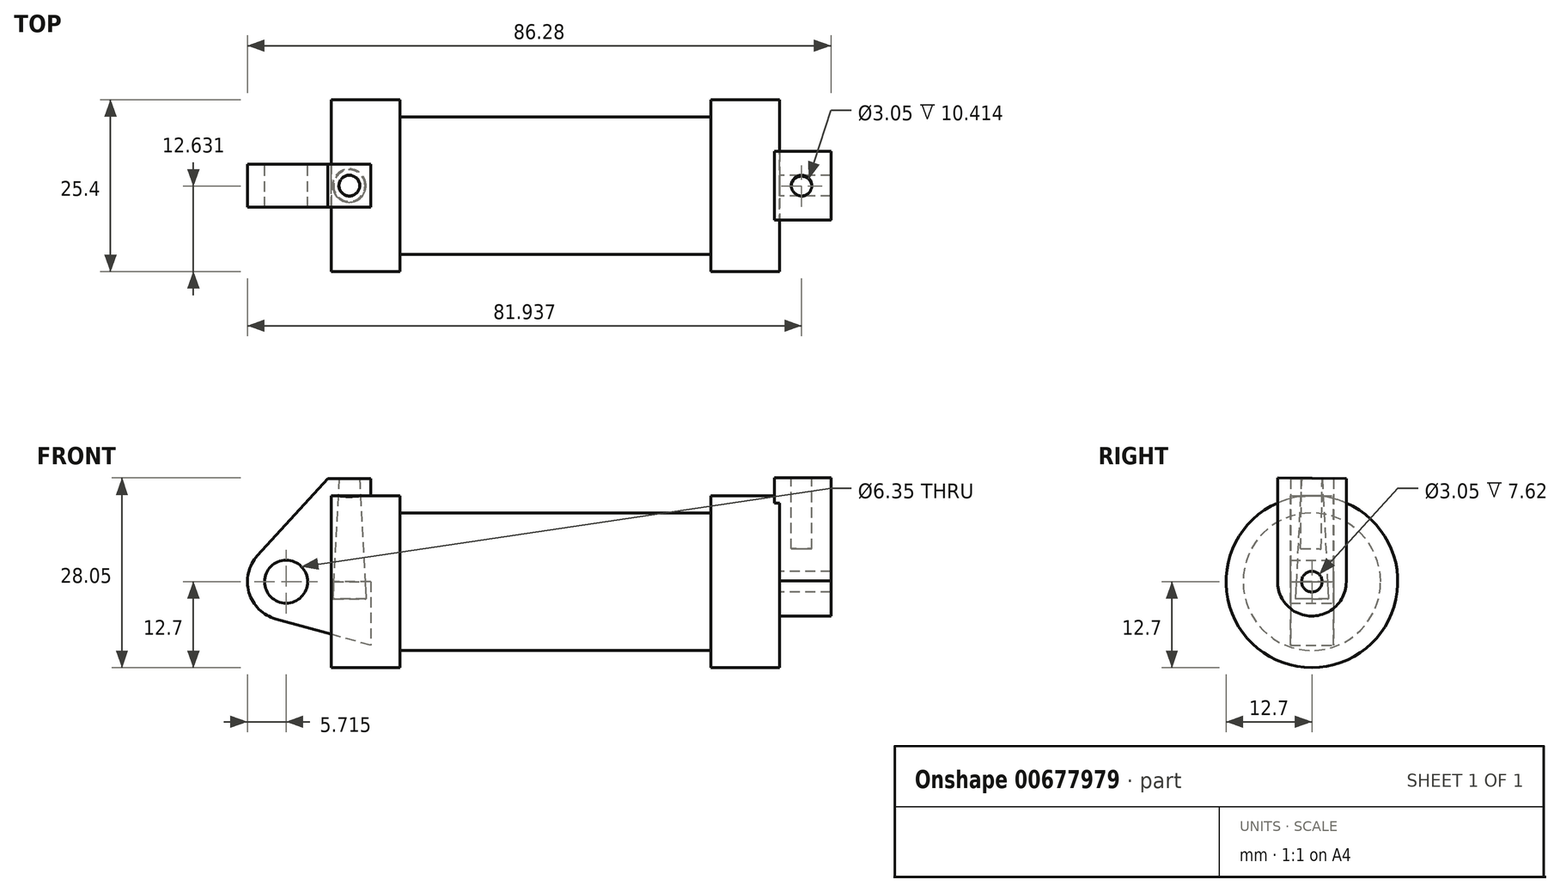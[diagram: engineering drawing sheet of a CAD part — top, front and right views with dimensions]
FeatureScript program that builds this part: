
annotation { "Feature Type Name" : "Feature", "Feature Type Description" : "" }
export const myFeature = defineFeature(function(context is Context, id is Id, definition is map)
    precondition{}
    {
        {
            var Q0;
            Q0=qCreatedBy(makeId("Front.planeOp"),FACE);
            var sketch = newSketch(context, id + "F0", { "sketchPlane" : qUnion([Q0])});
            skLineSegment(sketch, "E0", {"start": v(0, 0) * mm, "end": v(0, 12.7) * mm});
            skLineSegment(sketch, "E1", {"start": v(0, 12.7) * mm, "end": v(10.16, 12.7) * mm});
            skLineSegment(sketch, "E2", {"start": v(10.16, 12.7) * mm, "end": v(10.16, 10.16) * mm});
            skLineSegment(sketch, "E3", {"start": v(10.16, 10.16) * mm, "end": v(56.13, 10.16) * mm});
            skLineSegment(sketch, "E4", {"start": v(56.13, 10.16) * mm, "end": v(56.13, 12.7) * mm});
            skLineSegment(sketch, "E5", {"start": v(56.13, 12.7) * mm, "end": v(66.3, 12.7) * mm});
            skLineSegment(sketch, "E6", {"start": v(66.3, 12.7) * mm, "end": v(66.3, 0) * mm});
            skLineSegment(sketch, "E7", {"start": v(66.3, 0) * mm, "end": v(0, 0) * mm});
            skLineSegment(sketch, "E8", {"start": v(5.84, 15.24) * mm, "end": v(-0.5, 15.24) * mm});
            skLineSegment(sketch, "E9", {"start": v(-0.5, 15.24) * mm, "end": v(-10.88, 3.85) * mm});
            skLineSegment(sketch, "E10", {"start": v(0, 0) * mm, "end": v(-6.65, 0) * mm});
            skCircle(sketch, "E11", {"center": v(-6.65, 0) * mm, "radius": 5.72 * mm});
            skCircle(sketch, "E12", {"center": v(-6.65, 0) * mm, "radius": 3.18 * mm});
            skLineSegment(sketch, "E13", {"start": v(5.84, 15.24) * mm, "end": v(5.84, -9.4) * mm});
            skLineSegment(sketch, "E14", {"start": v(5.84, -9.4) * mm, "end": v(-8.18, -5.5) * mm});
            skSolve(sketch);
        }
        {
            var Q0;
            {var subQ0=sQuery(id+"F0.wireOp",EDGE,"E2");Q0=makeQuery(id+"F0.imprint","IMPRINT",FACE,{"disambiguationData":[TD([[makeQuery(id+"F0.imprint","IMPRINT",EDGE,{"derivedFrom":subQ0}),-1.0]])]});}
            var Q1;
            {var subQ0=sQuery(id+"F0.wireOp",EDGE,"E0");Q1=makeQuery(id+"F0.imprint","IMPRINT",FACE,{"disambiguationData":[TD([[makeQuery(id+"F0.imprint","IMPRINT",EDGE,{"derivedFrom":subQ0}),-1.0]])]});}
            var Q2;
            Q2=sQuery(id+"F0.wireOp",EDGE,"E7");
            revolve(context, id + "F1", {"entities" : qUnion([Q0, Q1]), "axis" : qUnion([Q2]), "revolveType" : RevolveType.FULL});
        }
        {
            var Q0;
            {var subQ1=sQuery(id+"F0.wireOp",EDGE,"E0");Q0=makeQuery(id+"F0.imprint","IMPRINT",FACE,{"disambiguationData":[TD([[makeQuery(id+"F0.imprint","IMPRINT",EDGE,{"derivedFrom":subQ1}),1.0]])]});}
            var Q1;
            {var subQ0=sQuery(id+"F0.wireOp",EDGE,"E14");Q1=makeQuery(id+"F0.imprint","IMPRINT",FACE,{"disambiguationData":[TD([[makeQuery(id+"F0.imprint","IMPRINT",EDGE,{"derivedFrom":subQ0}),-1.0]])]});}
            var Q2;
            {var subQ5=sQuery(id+"F0.wireOp",EDGE,"E12");Q2=makeQuery(id+"F0.imprint","IMPRINT",FACE,{"disambiguationData":[TD([[makeQuery(id+"F0.imprint","IMPRINT",EDGE,{"derivedFrom":subQ5}),-1.0]])]});}
            extrude(context, id + "F2", {"entities" : qUnion([Q0, Q1, Q2]), "endBound" : BoundingType.SYMMETRIC, "depth" : 6.35 * mm, "offsetDistance" : 25.4 * mm});
        }
        {
            var Q0;
            Q0=makeQuery(id+"F1.opRevolve","SWEPT_FACE",FACE,{"disambiguationData":[OSD([sQuery(id+"F0.wireOp",EDGE,"E6")])]});
            var sketch = newSketch(context, id + "F3", { "sketchPlane" : qUnion([Q0])});
            skCircle(sketch, "E15", {"center": v(0, 0) * mm, "radius": 1.52 * mm});
            skCircle(sketch, "E16", {"center": v(0, 0) * mm, "radius": 5.08 * mm});
            skLineSegment(sketch, "E17", {"start": v(-5.08, 0.11) * mm, "end": v(-5.08, 15.35) * mm});
            skLineSegment(sketch, "E18", {"start": v(5.08, -0.02) * mm, "end": v(5.08, 15.22) * mm});
            skLineSegment(sketch, "E19", {"start": v(5.08, 15.22) * mm, "end": v(-5.08, 15.35) * mm});
            skSolve(sketch);
        }
        {
            var Q0;
            Q0=makeQuery(id+"F3.imprint","IMPRINT",FACE,{"disambiguationData":[TD([[makeQuery(id+"F3.imprint","IMPRINT",EDGE,{"derivedFrom":sQuery(id+"F3.wireOp",EDGE,"E15")}),-1.0]])]});
            var Q1;
            {var subQ0=sQuery(id+"F3.wireOp",EDGE,"E19");Q1=makeQuery(id+"F3.imprint","IMPRINT",FACE,{"disambiguationData":[TD([[makeQuery(id+"F3.imprint","IMPRINT",EDGE,{"derivedFrom":subQ0}),1.0]])]});}
            var Q2;
            {var subQ0=sQuery(id+"F3.wireOp",EDGE,"E17");var subQ1=sQuery(id+"F3.wireOp",EDGE,"E16");var subQ2=makeQuery(id+"F3.imprint","INTERSECT",VERTEX,{"derivedFrom":[subQ1,subQ0]});Q2=makeQuery(id+"F3.imprint","IMPRINT",FACE,{"disambiguationData":[TD([[makeQuery(id+"F3.imprint","IMPRINT",EDGE,{"disambiguationData":[TD([[subQ2,1.0]])],"derivedFrom":subQ1}),-1.0]])]});}
            extrude(context, id + "F4", {"entities" : qUnion([Q0, Q1, Q2]), "operationType" : NewBodyOperationType.ADD, "depth" : 7.62 * mm, "offsetDistance" : 25.4 * mm, "hasSecondDirection" : true, "secondDirectionOppositeDirection" : true, "secondDirectionDepth" : 0.76 * mm});
        }
        {
            var Q0;
            Q0=makeQuery(id+"F2.opExtrude","SWEPT_FACE",FACE,{"disambiguationData":[OSD([sQuery(id+"F0.wireOp",EDGE,"E8")])]});
            var sketch = newSketch(context, id + "F5", { "sketchPlane" : qUnion([Q0])});
            skCircle(sketch, "E20", {"center": v(2.7, 0) * mm, "radius": 1.52 * mm});
            skPoint(sketch, "E20.centerSnap0", {"position": v(5.84, 0) * mm});
            skSolve(sketch);
        }
        {
            var Q0;
            Q0=makeQuery(id+"F5.imprint","IMPRINT",FACE,{"disambiguationData":[TD([[makeQuery(id+"F5.imprint","IMPRINT",EDGE,{"derivedFrom":sQuery(id+"F5.wireOp",EDGE,"E20")}),1.0]])]});
            var Q1;
            Q1=sQuery(id+"F5.wireOp",EDGE,"E20");
            extrude(context, id + "F6", {"entities" : qUnion([Q0]), "operationType" : NewBodyOperationType.REMOVE, "surfaceEntities" : qUnion([Q1]), "oppositeDirection" : true, "depth" : 17.78 * mm, "offsetDistance" : 25.4 * mm, "hasDraft" : true, "draftAngle" : 3 * degree});
        }
        {
            var Q0;
            Q0=makeQuery(id+"F4.opExtrude","SWEPT_FACE",FACE,{"disambiguationData":[OSD([sQuery(id+"F3.wireOp",EDGE,"E19")])]});
            var sketch = newSketch(context, id + "F7", { "sketchPlane" : qUnion([Q0])});
            skCircle(sketch, "E21", {"center": v(69.57, -0.2) * mm, "radius": 1.52 * mm});
            skPoint(sketch, "E21.centerSnap0", {"position": v(65.53, -0.2) * mm});
            skSolve(sketch);
        }
        {
            var Q0;
            Q0=makeQuery(id+"F7.imprint","IMPRINT",FACE,{"disambiguationData":[TD([[makeQuery(id+"F7.imprint","IMPRINT",EDGE,{"derivedFrom":sQuery(id+"F7.wireOp",EDGE,"E21")}),1.0]])]});
            extrude(context, id + "F8", {"entities" : qUnion([Q0]), "operationType" : NewBodyOperationType.REMOVE, "oppositeDirection" : true, "depth" : 10.4 * mm, "offsetDistance" : 25.4 * mm});
        }
    });
